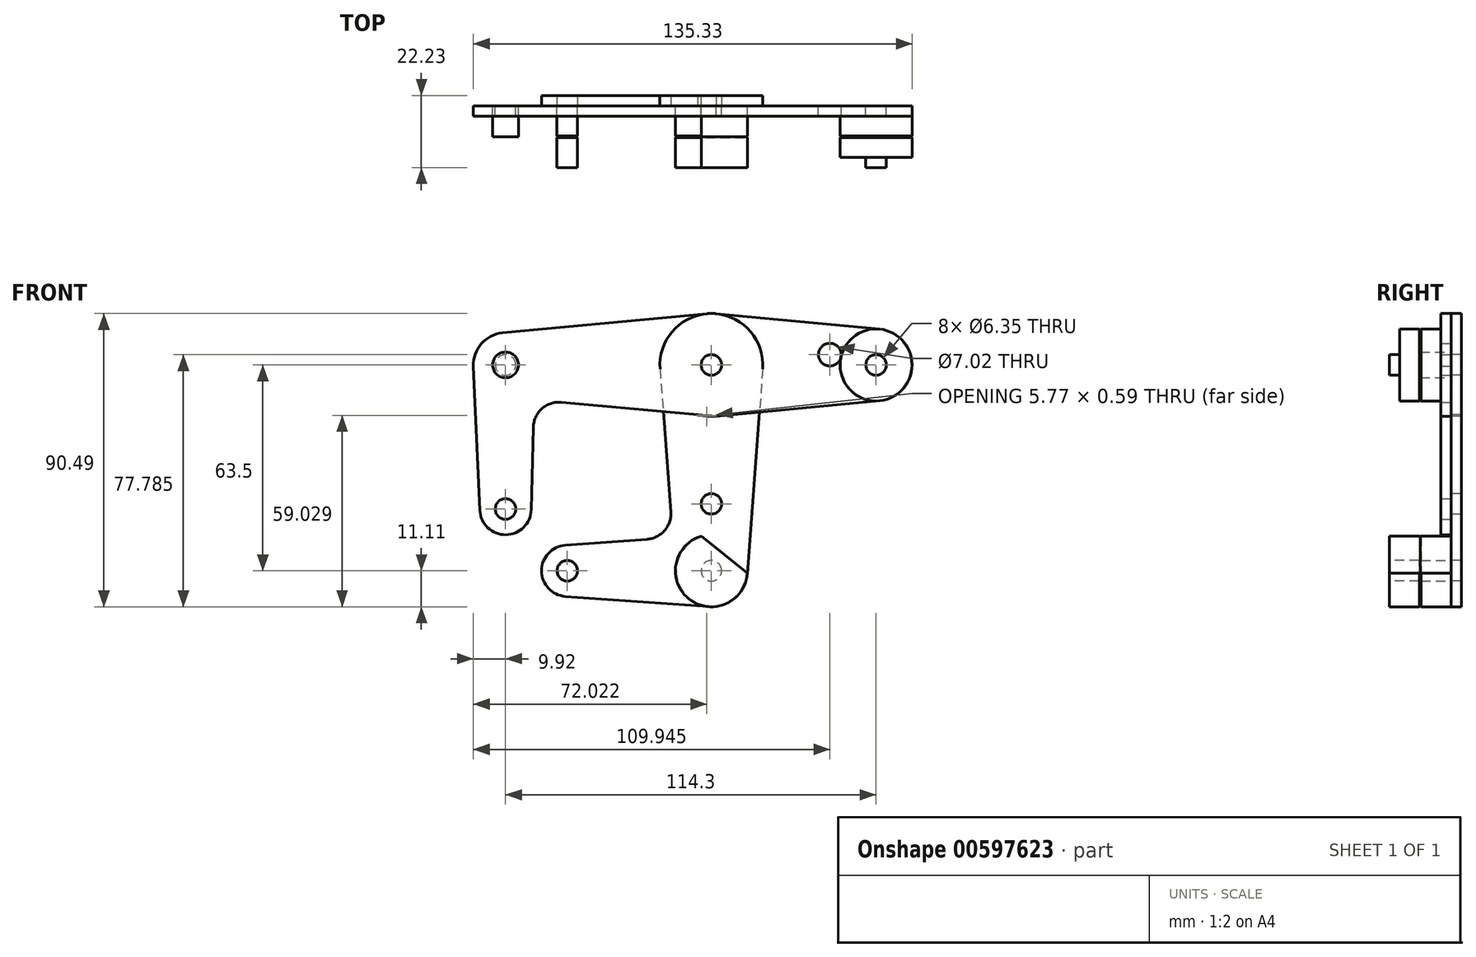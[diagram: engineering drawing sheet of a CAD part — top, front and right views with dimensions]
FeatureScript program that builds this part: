
annotation { "Feature Type Name" : "Feature", "Feature Type Description" : "" }
export const myFeature = defineFeature(function(context is Context, id is Id, definition is map)
    precondition{}
    {
        {
            var Q0;
            Q0=qCreatedBy(makeId("Front.planeOp"),FACE);
            var sketch = newSketch(context, id + "F0", { "sketchPlane" : qUnion([Q0])});
            skCircle(sketch, "E0", {"center": v(0, 0) * mm, "radius": 15.88 * mm});
            skCircle(sketch, "E1", {"center": v(0, 0) * mm, "radius": 3.18 * mm});
            skCircle(sketch, "E2", {"center": v(0, 0) * mm, "radius": 3.98 * mm});
            skCircle(sketch, "E3", {"center": v(50.8, 0) * mm, "radius": 11.11 * mm});
            skCircle(sketch, "E4", {"center": v(50.8, 0) * mm, "radius": 3.18 * mm});
            skCircle(sketch, "E5", {"center": v(-63.5, 0) * mm, "radius": 9.92 * mm});
            skCircle(sketch, "E6", {"center": v(-63.5, 0) * mm, "radius": 3.18 * mm});
            skCircle(sketch, "E7", {"center": v(-63.5, -44.45) * mm, "radius": 7.94 * mm});
            skCircle(sketch, "E8", {"center": v(-63.5, -44.45) * mm, "radius": 3.18 * mm});
            skPoint(sketch, "E9.first.point", {"position": v(39.69, 0) * mm});
            skPoint(sketch, "E9.second.point", {"position": v(39.87, 1.99) * mm});
            skCircle(sketch, "E10", {"center": v(36.53, 3.17) * mm, "radius": 3.51 * mm});
            skLineSegment(sketch, "E11", {"start": v(51.84, 11.06) * mm, "end": v(0, 15.95) * mm});
            skLineSegment(sketch, "E12", {"start": v(0, 15.95) * mm, "end": v(-64.43, 9.88) * mm});
            skLineSegment(sketch, "E13", {"start": v(-73.41, -0.44) * mm, "end": v(-71.43, -44.8) * mm});
            skLineSegment(sketch, "E14", {"start": v(51.84, -11.06) * mm, "end": v(1.49, -15.8) * mm});
            skLineSegment(sketch, "E15", {"start": v(1.49, -15.8) * mm, "end": v(-46.27, -11.51) * mm});
            skLineSegment(sketch, "E16", {"start": v(-55.56, -44.65) * mm, "end": v(-54.93, -19.23) * mm});
            skArc(sketch, "E17.filletArc", {"start": v(-46.27, -11.51) * mm, "mid": v(-52.27, -13.5) * mm, "end": v(-54.93, -19.23) * mm});
            skCircle(sketch, "E18", {"center": v(0, -63.5) * mm, "radius": 11.11 * mm});
            skCircle(sketch, "E19", {"center": v(0, -63.5) * mm, "radius": 3.18 * mm});
            skCircle(sketch, "E20", {"center": v(0, -42.85) * mm, "radius": 3.18 * mm});
            skCircle(sketch, "E21", {"center": v(-44.45, -63.5) * mm, "radius": 7.94 * mm});
            skCircle(sketch, "E22", {"center": v(-44.45, -63.5) * mm, "radius": 3.18 * mm});
            skLineSegment(sketch, "E23", {"start": v(15.83, -1.2) * mm, "end": v(11.08, -64.33) * mm});
            skLineSegment(sketch, "E24", {"start": v(-0.8, -74.58) * mm, "end": v(-45.02, -71.42) * mm});
            skLineSegment(sketch, "E25", {"start": v(-45.02, -55.58) * mm, "end": v(-19.88, -53.78) * mm});
            skLineSegment(sketch, "E26", {"start": v(-15.83, -1.2) * mm, "end": v(-12.52, -45.26) * mm});
            skArc(sketch, "E27.filletArc", {"start": v(-19.88, -53.78) * mm, "mid": v(-14.43, -51.05) * mm, "end": v(-12.52, -45.26) * mm});
            skLineSegment(sketch, "E28", {"start": v(-44.45, -63.5) * mm, "end": v(-63.5, -44.45) * mm, "construction": true});
            skLineSegment(sketch, "E29", {"start": v(-63.5, -44.45) * mm, "end": v(-63.5, -36.51) * mm, "construction": true});
            skLineSegment(sketch, "E30", {"start": v(-63.5, 0) * mm, "end": v(-63.5, -44.45) * mm, "construction": true});
            skLineSegment(sketch, "E31", {"start": v(-63.5, 0) * mm, "end": v(50.8, 0) * mm, "construction": true});
            skLineSegment(sketch, "E32", {"start": v(0, 0) * mm, "end": v(0, -63.5) * mm, "construction": true});
            skSolve(sketch);
        }
        {
            var Q0;
            Q0=makeQuery(id+"F0.imprint","IMPRINT",FACE,{"disambiguationData":[TD([[makeQuery(id+"F0.imprint","IMPRINT",EDGE,{"derivedFrom":sQuery(id+"F0.wireOp",EDGE,"E8")}),-1.0]])]});
            var Q1;
            {var subQ5=sQuery(id+"F0.wireOp",EDGE,"E13");Q1=makeQuery(id+"F0.imprint","IMPRINT",FACE,{"disambiguationData":[TD([[makeQuery(id+"F0.imprint","IMPRINT",EDGE,{"derivedFrom":subQ5}),1.0]])]});}
            var Q2;
            Q2=makeQuery(id+"F0.imprint","IMPRINT",FACE,{"disambiguationData":[TD([[makeQuery(id+"F0.imprint","IMPRINT",EDGE,{"derivedFrom":sQuery(id+"F0.wireOp",EDGE,"E6")}),-1.0]])]});
            var Q3;
            Q3=makeQuery(id+"F0.imprint","IMPRINT",FACE,{"disambiguationData":[TD([[makeQuery(id+"F0.imprint","IMPRINT",EDGE,{"derivedFrom":sQuery(id+"F0.wireOp",EDGE,"E2")}),-1.0]])]});
            var Q4;
            {var subQ3=sQuery(id+"F0.wireOp",EDGE,"E10");Q4=makeQuery(id+"F0.imprint","IMPRINT",FACE,{"disambiguationData":[TD([[makeQuery(id+"F0.imprint","IMPRINT",EDGE,{"derivedFrom":subQ3}),-1.0]])]});}
            var Q5;
            {var subQ1=sQuery(id+"F0.wireOp",EDGE,"E0");var subQ3=sQuery(id+"F0.wireOp",EDGE,"E23");var subQ4=makeQuery(id+"F0.imprint","INTERSECT",VERTEX,{"derivedFrom":[subQ1,subQ3]});Q5=makeQuery(id+"F0.imprint","IMPRINT",FACE,{"disambiguationData":[TD([[makeQuery(id+"F0.imprint","IMPRINT",EDGE,{"disambiguationData":[TD([[subQ4,-1.0]])],"derivedFrom":subQ3}),-1.0]])]});}
            var Q6;
            {var subQ0=sQuery(id+"F0.wireOp",EDGE,"E26");var subQ1=sQuery(id+"F0.wireOp",EDGE,"E0");var subQ2=makeQuery(id+"F0.imprint","INTERSECT",VERTEX,{"derivedFrom":[subQ1,subQ0]});Q6=makeQuery(id+"F0.imprint","IMPRINT",FACE,{"disambiguationData":[TD([[makeQuery(id+"F0.imprint","IMPRINT",EDGE,{"disambiguationData":[TD([[subQ2,-1.0]])],"derivedFrom":subQ1}),-1.0]])]});}
            var Q7;
            Q7=makeQuery(id+"F0.imprint","IMPRINT",FACE,{"disambiguationData":[TD([[makeQuery(id+"F0.imprint","IMPRINT",EDGE,{"derivedFrom":sQuery(id+"F0.wireOp",EDGE,"E4")}),-1.0]])]});
            var Q8;
            Q8=makeQuery(id+"F0.imprint","IMPRINT",FACE,{"disambiguationData":[TD([[makeQuery(id+"F0.imprint","IMPRINT",EDGE,{"derivedFrom":sQuery(id+"F0.wireOp",EDGE,"E1")}),-1.0]])]});
            extrude(context, id + "F1", {"entities" : qUnion([Q0, Q1, Q2, Q3, Q4, Q5, Q6, Q7, Q8]), "depth" : 3.17 * mm, "offsetDistance" : 25.4 * mm});
        }
        {
            var Q0;
            Q0=makeQuery(id+"F0.imprint","IMPRINT",FACE,{"disambiguationData":[TD([[makeQuery(id+"F0.imprint","IMPRINT",EDGE,{"derivedFrom":sQuery(id+"F0.wireOp",EDGE,"E20")}),-1.0]])]});
            var Q1;
            {var subQ1=sQuery(id+"F0.wireOp",EDGE,"E0");var subQ3=sQuery(id+"F0.wireOp",EDGE,"E23");var subQ4=makeQuery(id+"F0.imprint","INTERSECT",VERTEX,{"derivedFrom":[subQ1,subQ3]});Q1=makeQuery(id+"F0.imprint","IMPRINT",FACE,{"disambiguationData":[TD([[makeQuery(id+"F0.imprint","IMPRINT",EDGE,{"disambiguationData":[TD([[subQ4,-1.0]])],"derivedFrom":subQ3}),-1.0]])]});}
            var Q2;
            {var subQ0=sQuery(id+"F0.wireOp",EDGE,"E26");var subQ1=sQuery(id+"F0.wireOp",EDGE,"E0");var subQ2=makeQuery(id+"F0.imprint","INTERSECT",VERTEX,{"derivedFrom":[subQ1,subQ0]});Q2=makeQuery(id+"F0.imprint","IMPRINT",FACE,{"disambiguationData":[TD([[makeQuery(id+"F0.imprint","IMPRINT",EDGE,{"disambiguationData":[TD([[subQ2,-1.0]])],"derivedFrom":subQ1}),-1.0]])]});}
            var Q3;
            Q3=makeQuery(id+"F0.imprint","IMPRINT",FACE,{"disambiguationData":[TD([[makeQuery(id+"F0.imprint","IMPRINT",EDGE,{"derivedFrom":sQuery(id+"F0.wireOp",EDGE,"E2")}),-1.0]])]});
            var Q4;
            Q4=makeQuery(id+"F0.imprint","IMPRINT",FACE,{"disambiguationData":[TD([[makeQuery(id+"F0.imprint","IMPRINT",EDGE,{"derivedFrom":sQuery(id+"F0.wireOp",EDGE,"E1")}),-1.0]])]});
            var Q5;
            Q5=makeQuery(id+"F0.imprint","IMPRINT",FACE,{"disambiguationData":[TD([[makeQuery(id+"F0.imprint","IMPRINT",EDGE,{"derivedFrom":sQuery(id+"F0.wireOp",EDGE,"E19")}),-1.0]])]});
            var Q6;
            Q6=makeQuery(id+"F0.imprint","IMPRINT",FACE,{"disambiguationData":[TD([[makeQuery(id+"F0.imprint","IMPRINT",EDGE,{"derivedFrom":sQuery(id+"F0.wireOp",EDGE,"E22")}),-1.0]])]});
            extrude(context, id + "F2", {"entities" : qUnion([Q0, Q1, Q2, Q3, Q4, Q5, Q6]), "oppositeDirection" : true, "depth" : 3.17 * mm, "offsetDistance" : 25.4 * mm});
        }
        {
            var Q0;
            Q0=qCreatedBy(makeId("Front.planeOp"),FACE);
            var sketch = newSketch(context, id + "F3", { "sketchPlane" : qUnion([Q0])});
            skPoint(sketch, "E33.0", {"position": v(-63.5, 0) * mm});
            skCircle(sketch, "E34", {"center": v(-63.5, 0) * mm, "radius": 3.98 * mm});
            skPoint(sketch, "E35.0", {"position": v(50.8, 0) * mm});
            skCircle(sketch, "E36", {"center": v(50.8, 0) * mm, "radius": 11.11 * mm});
            skCircle(sketch, "E37", {"center": v(0, 0) * mm, "radius": 3.97 * mm});
            skSolve(sketch);
        }
        {
            var Q0;
            Q0=qCreatedBy(makeId("Front.planeOp"),FACE);
            var sketch = newSketch(context, id + "F4", { "sketchPlane" : qUnion([Q0])});
            skPoint(sketch, "E38.0", {"position": v(50.8, 0) * mm});
            skPoint(sketch, "E39.0", {"position": v(0, -42.85) * mm});
            skPoint(sketch, "E40.0", {"position": v(0, -63.5) * mm});
            skCircle(sketch, "E41.0", {"center": v(0, -63.5) * mm, "radius": 11.11 * mm});
            skLineSegment(sketch, "E42", {"start": v(0, -63.5) * mm, "end": v(50.8, 0) * mm, "construction": true});
            skLineSegment(sketch, "E43", {"start": v(0, -63.5) * mm, "end": v(3.97, -58.54) * mm, "construction": true});
            skLineSegment(sketch, "E44", {"start": v(-3.15, -52.84) * mm, "end": v(11.09, -64.24) * mm});
            skSolve(sketch);
        }
        {
            var Q0;
            Q0=qCreatedBy(makeId("Front.planeOp"),FACE);
            cPlane(context, id + "F5", {"entities" : qUnion([Q0]), "cplaneType" : CPlaneType.OFFSET, "offset" : 9.52 * mm, "width" : 152.4 * mm, "height" : 152.4 * mm});
        }
        {
            var Q0;
            Q0=makeQuery(id+"F0.imprint","IMPRINT",FACE,{"disambiguationData":[TD([[makeQuery(id+"F0.imprint","IMPRINT",EDGE,{"derivedFrom":sQuery(id+"F0.wireOp",EDGE,"E22")}),1.0]])]});
            var Q1;
            {var subQ0=sQuery(id+"F4.wireOp",EDGE,"E44");Q1=makeQuery(id+"F4.imprint","IMPRINT",FACE,{"disambiguationData":[TD([[makeQuery(id+"F4.imprint","IMPRINT",EDGE,{"derivedFrom":subQ0}),-1.0]])]});}
            var Q2;
            Q2=makeQuery(id+"F3.imprint","IMPRINT",FACE,{"disambiguationData":[TD([[makeQuery(id+"F3.imprint","IMPRINT",EDGE,{"derivedFrom":sQuery(id+"F3.wireOp",EDGE,"E36")}),1.0]])]});
            var Q3;
            Q3=makeQuery(id+"F3.imprint","IMPRINT",FACE,{"disambiguationData":[TD([[makeQuery(id+"F3.imprint","IMPRINT",EDGE,{"derivedFrom":sQuery(id+"F3.wireOp",EDGE,"E34")}),1.0]])]});
            var Q4;
            Q4=qCreatedBy(id+"F5.planeOp",FACE);
            extrude(context, id + "F6", {"entities" : qUnion([Q0, Q1, Q2, Q3]), "endBound" : BoundingType.UP_TO_SURFACE, "depth" : 25.4 * mm, "endBoundEntityFace" : qUnion([Q4]), "offsetDistance" : 25.4 * mm});
        }
        {
            var Q0;
            Q0=qCreatedBy(makeId("Front.planeOp"),FACE);
            var sketch = newSketch(context, id + "F7", { "sketchPlane" : qUnion([Q0])});
            skArc(sketch, "E45.0.0", {"start": v(-71.43, -44.8) * mm, "mid": v(-63.42, -52.39) * mm, "end": v(-55.56, -44.65) * mm});
            skLineSegment(sketch, "E45.0.1", {"start": v(-55.56, -44.65) * mm, "end": v(-54.93, -19.23) * mm});
            skArc(sketch, "E45.0.2", {"start": v(-54.93, -19.23) * mm, "mid": v(-52.27, -13.5) * mm, "end": v(-46.27, -11.51) * mm});
            skLineSegment(sketch, "E45.0.3", {"start": v(-46.27, -11.51) * mm, "end": v(1.49, -15.8) * mm});
            skLineSegment(sketch, "E45.0.4", {"start": v(1.49, -15.8) * mm, "end": v(51.84, -11.06) * mm});
            skArc(sketch, "E45.0.5", {"start": v(51.84, -11.06) * mm, "mid": v(61.91, 0) * mm, "end": v(51.84, 11.06) * mm});
            skLineSegment(sketch, "E45.0.6", {"start": v(51.84, 11.06) * mm, "end": v(1.49, 15.8) * mm});
            skArc(sketch, "E45.0.7", {"start": v(1.49, 15.8) * mm, "mid": v(0, 15.88) * mm, "end": v(-1.49, 15.8) * mm});
            skLineSegment(sketch, "E45.0.8", {"start": v(-1.49, 15.8) * mm, "end": v(-64.43, 9.88) * mm});
            skArc(sketch, "E45.0.9", {"start": v(-64.43, 9.88) * mm, "mid": v(-70.98, 6.51) * mm, "end": v(-73.41, -0.44) * mm});
            skLineSegment(sketch, "E45.0.10", {"start": v(-73.41, -0.44) * mm, "end": v(-71.43, -44.8) * mm});
            skLineSegment(sketch, "E46.0.0", {"start": v(11.08, -64.33) * mm, "end": v(14.83, -14.55) * mm});
            skLineSegment(sketch, "E46.0.1", {"start": v(14.83, -14.55) * mm, "end": v(1.49, -15.8) * mm});
            skArc(sketch, "E46.0.2", {"start": v(1.49, -15.8) * mm, "mid": v(-1.42, -15.81) * mm, "end": v(-4.28, -15.29) * mm});
            skLineSegment(sketch, "E46.0.3", {"start": v(-4.28, -15.29) * mm, "end": v(-14.84, -14.34) * mm});
            skLineSegment(sketch, "E46.0.4", {"start": v(-14.84, -14.34) * mm, "end": v(-12.52, -45.26) * mm});
            skArc(sketch, "E46.0.5", {"start": v(-12.52, -45.26) * mm, "mid": v(-14.43, -51.05) * mm, "end": v(-19.88, -53.78) * mm});
            skLineSegment(sketch, "E46.0.6", {"start": v(-19.88, -53.78) * mm, "end": v(-45.02, -55.58) * mm});
            skArc(sketch, "E46.0.7", {"start": v(-45.02, -55.58) * mm, "mid": v(-36.51, -63.5) * mm, "end": v(-45.02, -71.42) * mm});
            skLineSegment(sketch, "E46.0.8", {"start": v(-45.02, -71.42) * mm, "end": v(-0.8, -74.58) * mm});
            skArc(sketch, "E46.0.9", {"start": v(-0.8, -74.58) * mm, "mid": v(-7.26, -55.09) * mm, "end": v(11.08, -64.33) * mm});
            skCircle(sketch, "E47", {"center": v(0, 0) * mm, "radius": 3.98 * mm});
            skCircle(sketch, "E48", {"center": v(-63.5, 0) * mm, "radius": 3.98 * mm});
            skCircle(sketch, "E49", {"center": v(50.8, 0) * mm, "radius": 11.11 * mm});
            skSolve(sketch);
        }
        {
            var Q0;
            Q0=makeQuery(id+"F1.opExtrude","SWEPT_BODY",BODY,{"disambiguationData":[OSD([sQuery(id+"F0.wireOp",EDGE,"E0"),sQuery(id+"F0.wireOp",EDGE,"E1"),sQuery(id+"F0.wireOp",EDGE,"E3"),sQuery(id+"F0.wireOp",EDGE,"E4"),sQuery(id+"F0.wireOp",EDGE,"E5"),sQuery(id+"F0.wireOp",EDGE,"E6"),sQuery(id+"F0.wireOp",EDGE,"E7"),sQuery(id+"F0.wireOp",EDGE,"E8"),sQuery(id+"F0.wireOp",EDGE,"E10"),sQuery(id+"F0.wireOp",EDGE,"E11"),sQuery(id+"F0.wireOp",EDGE,"E12"),sQuery(id+"F0.wireOp",EDGE,"E13"),sQuery(id+"F0.wireOp",EDGE,"E14"),sQuery(id+"F0.wireOp",EDGE,"E15"),sQuery(id+"F0.wireOp",EDGE,"E16"),sQuery(id+"F0.wireOp",EDGE,"E17.filletArc")])]});
            var Q1;
            Q1=makeQuery(id+"F2.opExtrude","SWEPT_BODY",BODY,{"disambiguationData":[OSD([sQuery(id+"F0.wireOp",EDGE,"E0"),sQuery(id+"F0.wireOp",EDGE,"E1"),sQuery(id+"F0.wireOp",EDGE,"E15"),sQuery(id+"F0.wireOp",EDGE,"E18"),sQuery(id+"F0.wireOp",EDGE,"E19"),sQuery(id+"F0.wireOp",EDGE,"E20"),sQuery(id+"F0.wireOp",EDGE,"E21"),sQuery(id+"F0.wireOp",EDGE,"E22"),sQuery(id+"F0.wireOp",EDGE,"E23"),sQuery(id+"F0.wireOp",EDGE,"E24"),sQuery(id+"F0.wireOp",EDGE,"E25"),sQuery(id+"F0.wireOp",EDGE,"E26"),sQuery(id+"F0.wireOp",EDGE,"E27.filletArc")])]});
            var Q2;
            Q2=makeQuery(id+"F6.opExtrude","SWEPT_BODY",BODY,{"disambiguationData":[OSD([sQuery(id+"F3.wireOp",EDGE,"E36")])]});
            var Q3;
            Q3=makeQuery(id+"F6.opExtrude","SWEPT_BODY",BODY,{"disambiguationData":[OSD([sQuery(id+"F4.wireOp",EDGE,"E41.0"),sQuery(id+"F4.wireOp",EDGE,"E44")])]});
            var Q4;
            Q4=makeQuery(id+"F6.opExtrude","SWEPT_BODY",BODY,{"disambiguationData":[OSD([sQuery(id+"F0.wireOp",EDGE,"E6")])]});
            var Q5;
            Q5=makeQuery(id+"F6.opExtrude","SWEPT_BODY",BODY,{"disambiguationData":[OSD([sQuery(id+"F0.wireOp",EDGE,"E22")])]});
            booleanBodies(context, id + "F8", {"operationType" : BooleanOperationType.SUBTRACTION, "tools" : qUnion([Q0, Q1]), "targets" : qUnion([Q2, Q3, Q4, Q5]), "keepTools" : true});
        }
        {
            var Q0;
            Q0=makeQuery(id+"F6.opExtrude","CAP_EDGE",EDGE,{"disambiguationData":[OSD([sQuery(id+"F0.wireOp",EDGE,"E22")])],"isStart":false});
            var Q1;
            Q1=makeQuery(id+"F6.opExtrude","CAP_EDGE",EDGE,{"disambiguationData":[OSD([sQuery(id+"F4.wireOp",EDGE,"E41.0")])],"isStart":false});
            var Q2;
            Q2=makeQuery(id+"F6.opExtrude","CAP_EDGE",EDGE,{"disambiguationData":[OSD([sQuery(id+"F3.wireOp",EDGE,"E36")])],"isStart":false});
            var Q3;
            Q3=makeQuery(id+"F6.opExtrude","TWEAK_EDGE",EDGE,{"derivedFrom":[makeQuery(id+"F0.imprint","IMPRINT",EDGE,{"derivedFrom":sQuery(id+"F0.wireOp",EDGE,"E6")}),dummyQuery(id+"F5.planeOp",FACE)]});
            chamfer(context, id + "F9", {"entities" : qUnion([Q0, Q1, Q2, Q3]), "width" : 0.25 * mm, "tangentPropagation" : true});
        }
        {
            var Q0;
            Q0=makeQuery(id+"F6.opExtrude","SWEPT_BODY",BODY,{"disambiguationData":[OSD([sQuery(id+"F4.wireOp",EDGE,"E41.0"),sQuery(id+"F4.wireOp",EDGE,"E44")])]});
            var Q1;
            Q1=makeQuery(id+"F6.opExtrude","SWEPT_BODY",BODY,{"disambiguationData":[OSD([sQuery(id+"F3.wireOp",EDGE,"E36")])]});
            var Q2;
            Q2=qCreatedBy(id+"F5.planeOp",FACE);
            mirror(context, id + "F10", {"entities" : qUnion([Q0, Q1]), "mirrorPlane" : qUnion([Q2])});
        }
        {
            var Q0;
            Q0=qCreatedBy(makeId("Front.planeOp"),FACE);
            var sketch = newSketch(context, id + "F11", { "sketchPlane" : qUnion([Q0])});
            skCircle(sketch, "E50.0", {"center": v(0, -63.5) * mm, "radius": 3.18 * mm});
            skSolve(sketch);
        }
        {
            var Q0;
            Q0=sQuery(id+"F11.wireOp",EDGE,"E50.0");
            extrude(context, id + "F12", {"bodyType" : ToolBodyType.SURFACE, "surfaceEntities" : qUnion([Q0]), "depth" : 22.22 * mm, "offsetDistance" : 25.4 * mm});
        }
        {
            var Q0;
            Q0=sQuery(id+"F7.wireOp",EDGE,"E48");
            var Q1;
            Q1=qCreatedBy(id+"F5.planeOp",FACE);
            extrude(context, id + "F13", {"bodyType" : ToolBodyType.SURFACE, "surfaceEntities" : qUnion([Q0]), "endBound" : BoundingType.UP_TO_SURFACE, "depth" : 22.22 * mm, "endBoundEntityFace" : qUnion([Q1]), "offsetDistance" : 25.4 * mm});
        }
        {
            var Q0;
            Q0=makeQuery(id+"F6.opExtrude","SWEPT_BODY",BODY,{"disambiguationData":[OSD([sQuery(id+"F0.wireOp",EDGE,"E22")])]});
            var Q1;
            Q1=makeQuery(id+"F13.opExtrude","SWEPT_BODY",BODY,{"disambiguationData":[OSD([sQuery(id+"F7.wireOp",EDGE,"E48")])]});
            var Q2;
            Q2=qCreatedBy(id+"F5.planeOp",FACE);
            mirror(context, id + "F14", {"operationType" : NewBodyOperationType.ADD, "entities" : qUnion([Q0, Q1]), "mirrorPlane" : qUnion([Q2])});
        }
        {
            var Q0;
            Q0=sQuery(id+"F0.wireOp",EDGE,"E6");
            extrude(context, id + "F15", {"bodyType" : ToolBodyType.SURFACE, "surfaceEntities" : qUnion([Q0]), "depth" : 22.22 * mm, "offsetDistance" : 25.4 * mm});
        }
        {
            var Q0;
            Q0=makeQuery(id+"F13.opExtrude","SWEPT_BODY",BODY,{"disambiguationData":[OSD([sQuery(id+"F7.wireOp",EDGE,"E48")])]});
            var Q1;
            Q1=qCreatedBy(id+"F5.planeOp",FACE);
            mirror(context, id + "F16", {"entities" : qUnion([Q0]), "mirrorPlane" : qUnion([Q1])});
        }
    });
